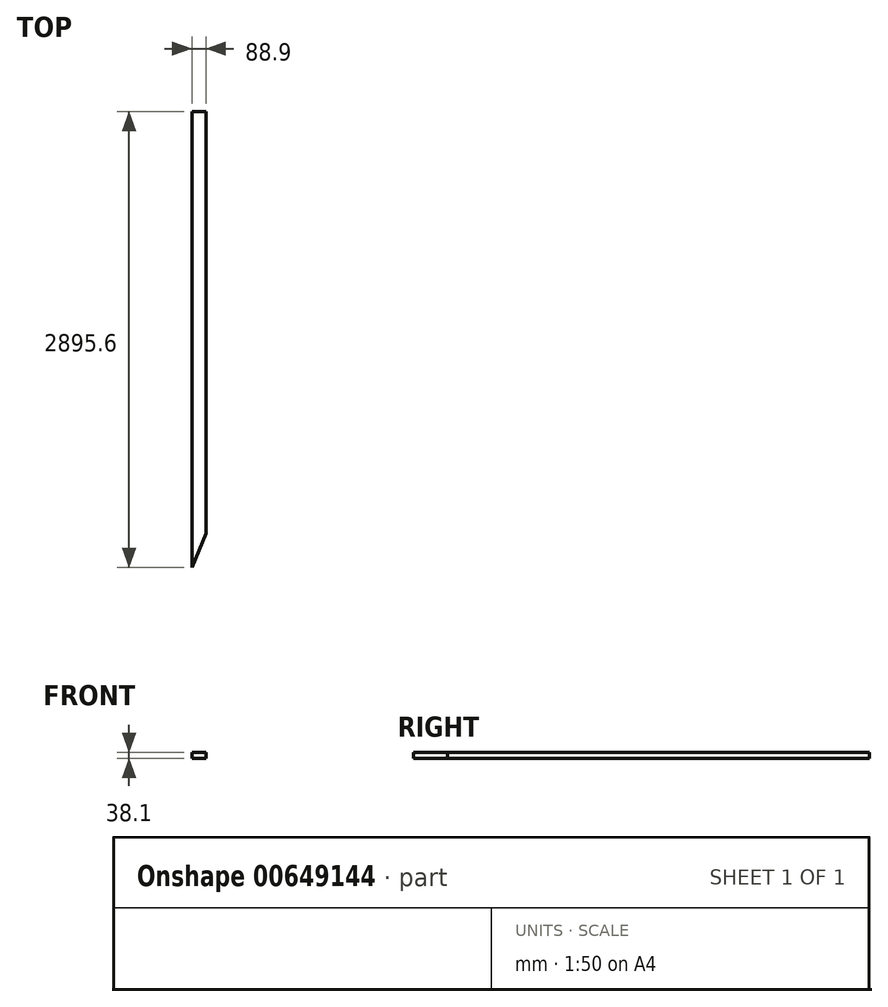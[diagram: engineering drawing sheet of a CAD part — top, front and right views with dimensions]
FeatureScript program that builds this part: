
annotation { "Feature Type Name" : "Feature", "Feature Type Description" : "" }
export const myFeature = defineFeature(function(context is Context, id is Id, definition is map)
    precondition{}
    {
        {
            var Q0;
            Q0=qCreatedBy(makeId("Front.planeOp"),FACE);
            var sketch = newSketch(context, id + "F0", { "sketchPlane" : qUnion([Q0])});
            skLineSegment(sketch, "E0.bottom", {"start": v(0, 0) * mm, "end": v(88.9, 0) * mm});
            skLineSegment(sketch, "E0.top", {"start": v(0, 38.1) * mm, "end": v(88.9, 38.1) * mm});
            skLineSegment(sketch, "E0.left", {"start": v(0, 0) * mm, "end": v(0, 38.1) * mm});
            skLineSegment(sketch, "E0.right", {"start": v(88.9, 0) * mm, "end": v(88.9, 38.1) * mm});
            skSolve(sketch);
        }
        {
            var Q0;
            Q0 = qSketchRegion(id + "F0", true);
            extrude(context, id + "F1", {"entities" : qUnion([Q0]), "depth" : 19 / 2 * 304.8 * mm, "offsetDistance" : 25.4 * mm});
        }
        {
            var Q0;
            Q0=makeQuery(id+"F1.opExtrude","SWEPT_FACE",FACE,{"disambiguationData":[OSD([sQuery(id+"F0.wireOp",EDGE,"E0.top")])]});
            var sketch = newSketch(context, id + "F2", { "sketchPlane" : qUnion([Q0])});
            skLineSegment(sketch, "E1", {"start": v(0, -2895.6) * mm, "end": v(88.9, -2680.98) * mm});
            skLineSegment(sketch, "E2", {"start": v(88.9, -2680.98) * mm, "end": v(88.9, -2895.6) * mm});
            skLineSegment(sketch, "E3", {"start": v(88.9, -2895.6) * mm, "end": v(0, -2895.6) * mm});
            skSolve(sketch);
        }
        {
            var Q0;
            Q0 = qSketchRegion(id + "F2", true);
            extrude(context, id + "F3", {"entities" : qUnion([Q0]), "operationType" : NewBodyOperationType.REMOVE, "endBound" : BoundingType.UP_TO_NEXT, "oppositeDirection" : true, "depth" : 25.4 * mm, "offsetDistance" : 25.4 * mm});
        }
    });
